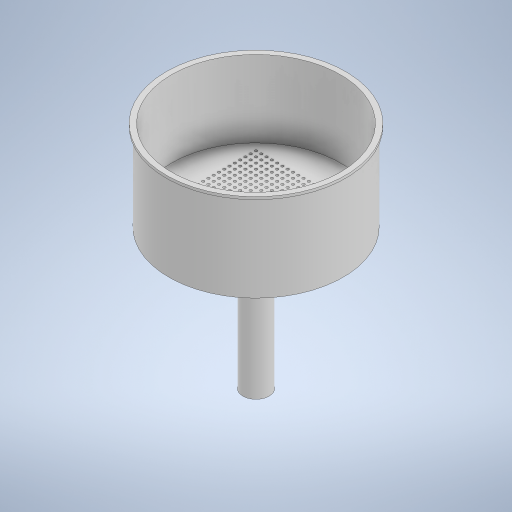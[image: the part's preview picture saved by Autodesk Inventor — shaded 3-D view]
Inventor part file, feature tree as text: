
AUTODESK INVENTOR PART (.ipt)
format: ipt  version: 2024 (Build 280153000, 153)  size: 609,792 bytes
history: native  units: mm
features: sketch x5, extrude x2, hole x2, revolve x1, shell x1, plane x1, pattern_linear x1
ambient origin geometry x8: Origin, YZ Plane, XZ Plane, XY Plane, X Axis, Y Axis, Z Axis, Center Point
bodies: Solid1 (feature_tree)
feature tree (13):
  revolve  "Revolution1"  [1 undecoded]
  shell  "Shell1"  Thickness=1.0mm
  extrude  "Extrusion1"  Depth=1.0mm
  hole  "Hole1"  [1 undecoded]
  plane  "Work Plane1"
  extrude  "Extrusion2"  Depth=10.0mm
  hole  "Hole2"  [1 undecoded]
  pattern_linear  "Rectangular Pattern1"  Spacing1=64.0mm  [1 undecoded]
  sketch  "Sketch1"  dims[d0=34.0mm d2=42.0mm d3=1.0mm]
  sketch  "Sketch2"  dims[d5=5.0mm d8=1.0mm]
  sketch  "Sketch3"  dims[d9=8.0mm d10=90.0deg]
  sketch  "Sketch4"  dims[d11=1.0mm d12=10.0mm]
  sketch  "Sketch5"  dims[d13=45.0mm d14=0.0mm d15=8.0mm d16=6.0mm d17=4.0mm d18=2.0mm d19=90.0deg d20=8.0mm d21=20.594885mm d22=-30.0mm d23=64.0mm d24=1.0mm d25=0.0mm d26=20.0mm d27=20.0mm d28=1.0mm d29=6.0mm d30=4.0mm d31=2.0mm d32=90.0deg d33=1.0mm d34=20.594885mm d35=210.0mm d37=2.0mm d38=210.0mm d40=2.0mm]
note: 4 required parameter values undecoded (feature->parameter linkage not recoverable at this tier; creation-order binding heuristic only, values carry confidence <= 0.55)